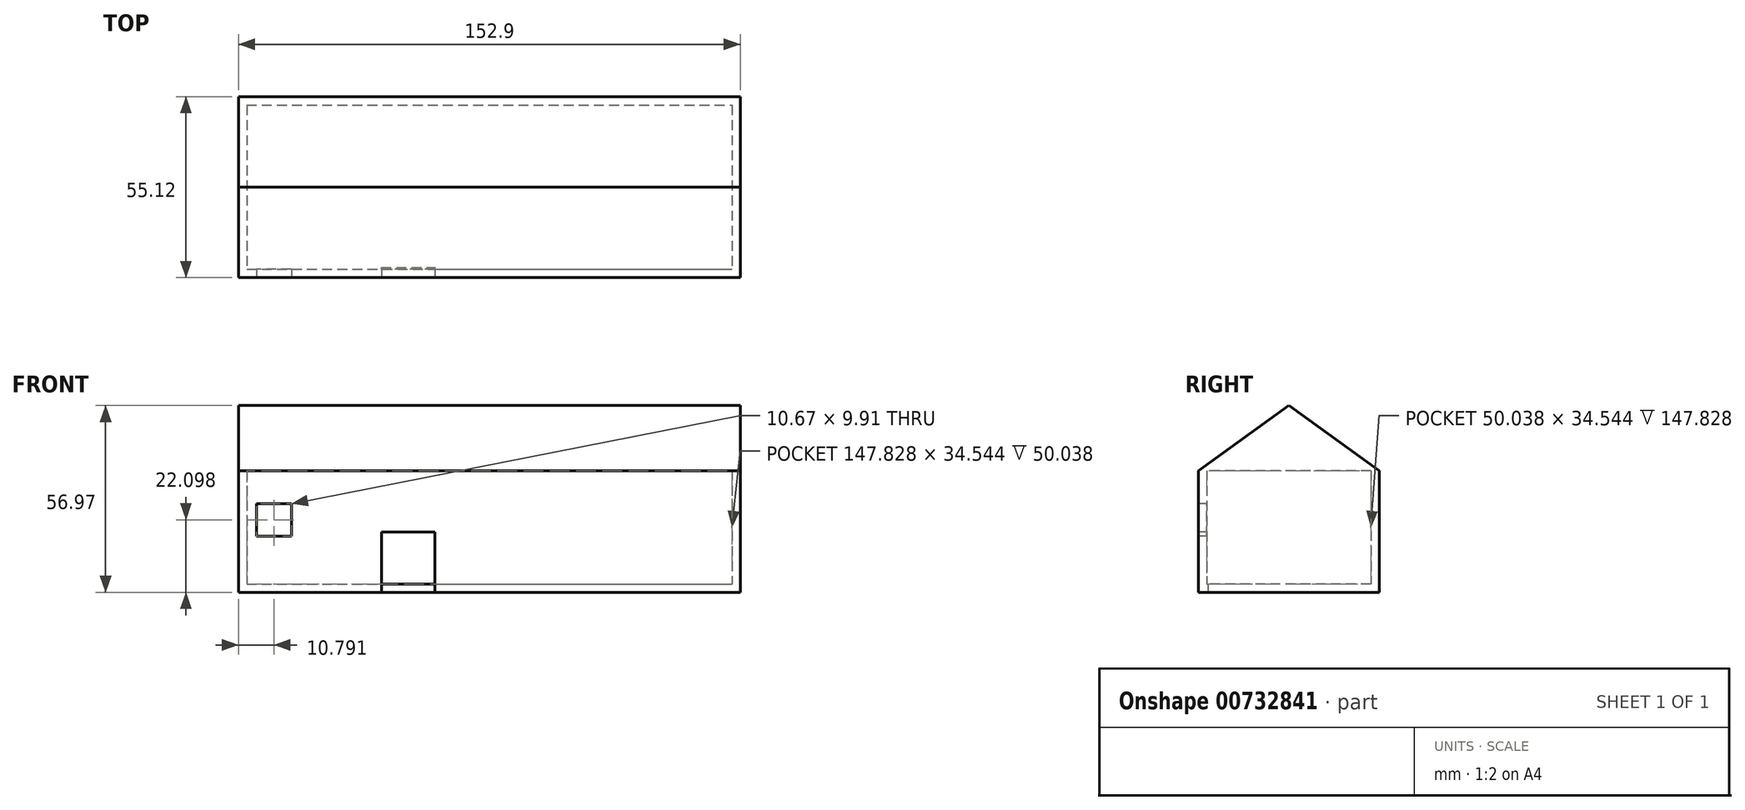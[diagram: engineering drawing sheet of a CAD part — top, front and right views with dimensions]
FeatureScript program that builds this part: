
annotation { "Feature Type Name" : "Feature", "Feature Type Description" : "" }
export const myFeature = defineFeature(function(context is Context, id is Id, definition is map)
    precondition{}
    {
        {
            var Q0;
            Q0=qCreatedBy(makeId("Top.planeOp"),FACE);
            var sketch = newSketch(context, id + "F0", { "sketchPlane" : qUnion([Q0])});
            skLineSegment(sketch, "E0.bottom", {"start": v(-76.45, 27.56) * mm, "end": v(76.45, 27.56) * mm});
            skLineSegment(sketch, "E0.top", {"start": v(-76.45, -27.56) * mm, "end": v(76.45, -27.56) * mm});
            skLineSegment(sketch, "E0.left", {"start": v(-76.45, 27.56) * mm, "end": v(-76.45, -27.56) * mm});
            skLineSegment(sketch, "E0.right", {"start": v(76.45, 27.56) * mm, "end": v(76.45, -27.56) * mm});
            skPoint(sketch, "E0.middle", {"position": v(0, 0) * mm});
            skSolve(sketch);
        }
        {
            var Q0;
            Q0=makeQuery(id+"F0.imprint","IMPRINT",FACE,{"disambiguationData":[TD([[makeQuery(id+"F0.imprint","IMPRINT",EDGE,{"derivedFrom":sQuery(id+"F0.wireOp",EDGE,"E0.bottom")}),-1.0]])]});
            extrude(context, id + "F1", {"entities" : qUnion([Q0]), "depth" : 37.08 * mm, "offsetDistance" : 25.4 * mm});
        }
        {
            var Q0;
            Q0=makeQuery(id+"F1.opExtrude","CAP_FACE",FACE,{"disambiguationData":[OSD([sQuery(id+"F0.wireOp",EDGE,"E0.bottom"),sQuery(id+"F0.wireOp",EDGE,"E0.top"),sQuery(id+"F0.wireOp",EDGE,"E0.left"),sQuery(id+"F0.wireOp",EDGE,"E0.right")])],"isStart":false});
            shell(context, id + "F2", {"entities" : qUnion([Q0]), "thickness" : 2.54 * mm});
        }
        {
            var Q0;
            Q0=makeQuery(id+"F1.opExtrude","SWEPT_FACE",FACE,{"disambiguationData":[OSD([sQuery(id+"F0.wireOp",EDGE,"E0.top")])]});
            var sketch = newSketch(context, id + "F3", { "sketchPlane" : qUnion([Q0])});
            skLineSegment(sketch, "E1.bottom", {"start": v(-32.9, 0) * mm, "end": v(-16.64, 0) * mm});
            skLineSegment(sketch, "E1.top", {"start": v(-32.9, 18.42) * mm, "end": v(-16.64, 18.42) * mm});
            skLineSegment(sketch, "E1.left", {"start": v(-32.9, 0) * mm, "end": v(-32.9, 18.42) * mm});
            skLineSegment(sketch, "E1.right", {"start": v(-16.64, 0) * mm, "end": v(-16.64, 18.42) * mm});
            skSolve(sketch);
        }
        {
            var Q0;
            Q0=makeQuery(id+"F3.imprint","IMPRINT",FACE,{"disambiguationData":[TD([[makeQuery(id+"F3.imprint","IMPRINT",EDGE,{"derivedFrom":sQuery(id+"F3.wireOp",EDGE,"E1.bottom")}),1.0]])]});
            extrude(context, id + "F4", {"entities" : qUnion([Q0]), "operationType" : NewBodyOperationType.REMOVE, "oppositeDirection" : true, "depth" : 3.05 * mm, "offsetDistance" : 25.4 * mm});
        }
        {
            var Q0;
            Q0=makeQuery(id+"F1.opExtrude","SWEPT_FACE",FACE,{"disambiguationData":[OSD([sQuery(id+"F0.wireOp",EDGE,"E0.right")])]});
            var sketch = newSketch(context, id + "F5", { "sketchPlane" : qUnion([Q0])});
            skLineSegment(sketch, "E2", {"start": v(0, 56.97) * mm, "end": v(-27.56, 37.08) * mm});
            skLineSegment(sketch, "E3", {"start": v(0, 56.97) * mm, "end": v(27.56, 37.08) * mm});
            skSolve(sketch);
        }
        {
            var Q0;
            Q0=makeQuery(id+"F5.imprint","IMPRINT",FACE,{"disambiguationData":[TD([[makeQuery(id+"F5.imprint","IMPRINT",EDGE,{"derivedFrom":sQuery(id+"F5.wireOp",EDGE,"E2")}),1.0]])]});
            extrude(context, id + "F6", {"entities" : qUnion([Q0]), "operationType" : NewBodyOperationType.ADD, "oppositeDirection" : true, "depth" : 152.9 * mm, "offsetDistance" : 25.4 * mm});
        }
        {
            var Q0;
            Q0=makeQuery(id+"F1.opExtrude","SWEPT_FACE",FACE,{"disambiguationData":[OSD([sQuery(id+"F0.wireOp",EDGE,"E0.top")])]});
            var sketch = newSketch(context, id + "F7", { "sketchPlane" : qUnion([Q0])});
            skLineSegment(sketch, "E4.bottom", {"start": v(-71, 27.05) * mm, "end": v(-60.33, 27.05) * mm});
            skLineSegment(sketch, "E4.top", {"start": v(-71, 17.15) * mm, "end": v(-60.33, 17.15) * mm});
            skLineSegment(sketch, "E4.left", {"start": v(-71, 27.05) * mm, "end": v(-71, 17.15) * mm});
            skLineSegment(sketch, "E4.right", {"start": v(-60.33, 27.05) * mm, "end": v(-60.33, 17.15) * mm});
            skSolve(sketch);
        }
        {
            var Q0;
            Q0=makeQuery(id+"F7.imprint","IMPRINT",FACE,{"disambiguationData":[TD([[makeQuery(id+"F7.imprint","IMPRINT",EDGE,{"derivedFrom":sQuery(id+"F7.wireOp",EDGE,"E4.bottom")}),-1.0]])]});
            extrude(context, id + "F8", {"entities" : qUnion([Q0]), "operationType" : NewBodyOperationType.REMOVE, "oppositeDirection" : true, "depth" : 2.8 * mm, "offsetDistance" : 25.4 * mm});
        }
    });
